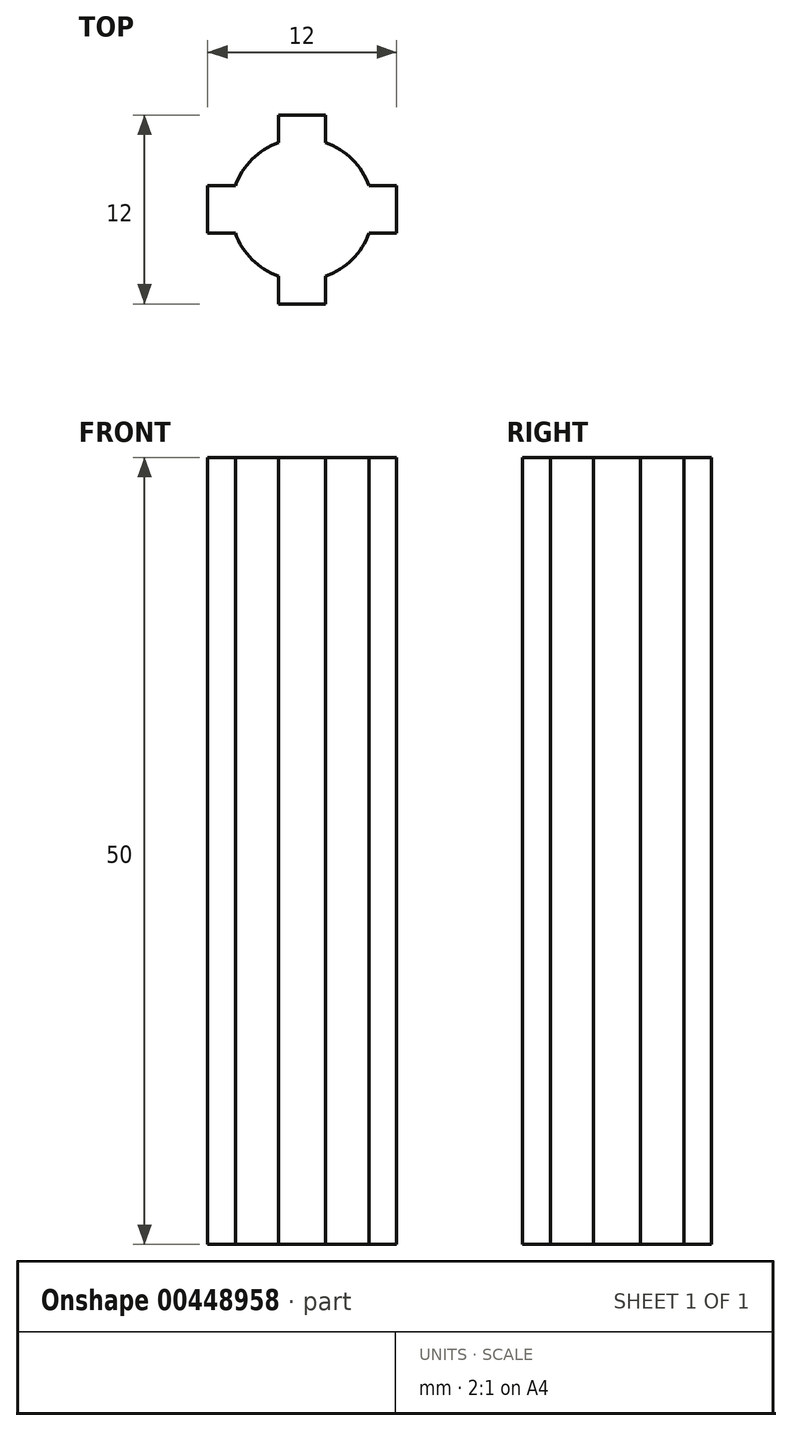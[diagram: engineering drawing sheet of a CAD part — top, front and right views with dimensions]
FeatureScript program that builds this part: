
annotation { "Feature Type Name" : "Feature", "Feature Type Description" : "" }
export const myFeature = defineFeature(function(context is Context, id is Id, definition is map)
    precondition{}
    {
        {
            var Q0;
            Q0=qCreatedBy(makeId("Top.planeOp"),FACE);
            var sketch = newSketch(context, id + "F0", { "sketchPlane" : qUnion([Q0])});
            skCircle(sketch, "E0", {"center": v(0, 0) * mm, "radius": 4.5 * mm});
            skLineSegment(sketch, "E1.bottom", {"start": v(6, -1.5) * mm, "end": v(-6, -1.5) * mm});
            skLineSegment(sketch, "E1.top", {"start": v(6, 1.5) * mm, "end": v(-6, 1.5) * mm});
            skLineSegment(sketch, "E1.left", {"start": v(6, -1.5) * mm, "end": v(6, 1.5) * mm});
            skLineSegment(sketch, "E1.right", {"start": v(-6, -1.5) * mm, "end": v(-6, 1.5) * mm});
            skLineSegment(sketch, "E2.bottom", {"start": v(-1.5, 6) * mm, "end": v(1.5, 6) * mm});
            skLineSegment(sketch, "E2.top", {"start": v(-1.5, -6) * mm, "end": v(1.5, -6) * mm});
            skLineSegment(sketch, "E2.left", {"start": v(-1.5, 6) * mm, "end": v(-1.5, -6) * mm});
            skLineSegment(sketch, "E2.right", {"start": v(1.5, 6) * mm, "end": v(1.5, -6) * mm});
            skSolve(sketch);
        }
        {
            var Q0;
            {var subQ5=sQuery(id+"F0.wireOp",EDGE,"E2.bottom");Q0=makeQuery(id+"F0.imprint","IMPRINT",FACE,{"disambiguationData":[TD([[makeQuery(id+"F0.imprint","IMPRINT",EDGE,{"derivedFrom":subQ5}),-1.0]])]});}
            var Q1;
            {var subQ5=sQuery(id+"F0.wireOp",EDGE,"E2.top");Q1=makeQuery(id+"F0.imprint","IMPRINT",FACE,{"disambiguationData":[TD([[makeQuery(id+"F0.imprint","IMPRINT",EDGE,{"derivedFrom":subQ5}),1.0]])]});}
            var Q2;
            {var subQ0=sQuery(id+"F0.wireOp",EDGE,"E2.right");var subQ1=sQuery(id+"F0.wireOp",EDGE,"E1.bottom");var subQ2=makeQuery(id+"F0.imprint","INTERSECT",VERTEX,{"derivedFrom":[subQ1,subQ0]});Q2=makeQuery(id+"F0.imprint","IMPRINT",FACE,{"disambiguationData":[TD([[makeQuery(id+"F0.imprint","IMPRINT",EDGE,{"disambiguationData":[TD([[subQ2,-1.0]])],"derivedFrom":subQ1}),-1.0]])]});}
            var Q3;
            {var subQ0=sQuery(id+"F0.wireOp",EDGE,"E2.left");var subQ1=sQuery(id+"F0.wireOp",EDGE,"E0");var subQ2=makeQuery(id+"F0.imprint","INTERSECT",VERTEX,{"disambiguationData":[OD(1.0)],"derivedFrom":[subQ1,subQ0]});Q3=makeQuery(id+"F0.imprint","IMPRINT",FACE,{"disambiguationData":[TD([[makeQuery(id+"F0.imprint","IMPRINT",EDGE,{"disambiguationData":[TD([[subQ2,-1.0]])],"derivedFrom":subQ1}),1.0]])]});}
            var Q4;
            {var subQ0=sQuery(id+"F0.wireOp",EDGE,"E2.right");var subQ1=sQuery(id+"F0.wireOp",EDGE,"E0");var subQ2=makeQuery(id+"F0.imprint","INTERSECT",VERTEX,{"disambiguationData":[OD(0.0)],"derivedFrom":[subQ1,subQ0]});Q4=makeQuery(id+"F0.imprint","IMPRINT",FACE,{"disambiguationData":[TD([[makeQuery(id+"F0.imprint","IMPRINT",EDGE,{"disambiguationData":[TD([[subQ2,-1.0]])],"derivedFrom":subQ1}),1.0]])]});}
            var Q5;
            {var subQ0=sQuery(id+"F0.wireOp",EDGE,"E2.right");var subQ1=sQuery(id+"F0.wireOp",EDGE,"E0");var subQ2=makeQuery(id+"F0.imprint","INTERSECT",VERTEX,{"disambiguationData":[OD(0.0)],"derivedFrom":[subQ1,subQ0]});Q5=makeQuery(id+"F0.imprint","IMPRINT",FACE,{"disambiguationData":[TD([[makeQuery(id+"F0.imprint","IMPRINT",EDGE,{"disambiguationData":[TD([[subQ2,1.0]])],"derivedFrom":subQ1}),1.0]])]});}
            var Q6;
            {var subQ0=sQuery(id+"F0.wireOp",EDGE,"E1.top");var subQ1=sQuery(id+"F0.wireOp",EDGE,"E0");var subQ2=makeQuery(id+"F0.imprint","INTERSECT",VERTEX,{"disambiguationData":[OD(0.0)],"derivedFrom":[subQ1,subQ0]});Q6=makeQuery(id+"F0.imprint","IMPRINT",FACE,{"disambiguationData":[TD([[makeQuery(id+"F0.imprint","IMPRINT",EDGE,{"disambiguationData":[TD([[subQ2,1.0]])],"derivedFrom":subQ1}),1.0]])]});}
            var Q7;
            {var subQ0=sQuery(id+"F0.wireOp",EDGE,"E2.right");var subQ1=sQuery(id+"F0.wireOp",EDGE,"E0");var subQ2=makeQuery(id+"F0.imprint","INTERSECT",VERTEX,{"disambiguationData":[OD(1.0)],"derivedFrom":[subQ1,subQ0]});Q7=makeQuery(id+"F0.imprint","IMPRINT",FACE,{"disambiguationData":[TD([[makeQuery(id+"F0.imprint","IMPRINT",EDGE,{"disambiguationData":[TD([[subQ2,-1.0]])],"derivedFrom":subQ1}),1.0]])]});}
            var Q8;
            {var subQ0=sQuery(id+"F0.wireOp",EDGE,"E1.bottom");var subQ1=sQuery(id+"F0.wireOp",EDGE,"E0");var subQ2=makeQuery(id+"F0.imprint","INTERSECT",VERTEX,{"disambiguationData":[OD(0.0)],"derivedFrom":[subQ1,subQ0]});Q8=makeQuery(id+"F0.imprint","IMPRINT",FACE,{"disambiguationData":[TD([[makeQuery(id+"F0.imprint","IMPRINT",EDGE,{"disambiguationData":[TD([[subQ2,-1.0]])],"derivedFrom":subQ1}),1.0]])]});}
            var Q9;
            {var subQ0=sQuery(id+"F0.wireOp",EDGE,"E1.top");var subQ1=sQuery(id+"F0.wireOp",EDGE,"E0");var subQ2=makeQuery(id+"F0.imprint","INTERSECT",VERTEX,{"disambiguationData":[OD(1.0)],"derivedFrom":[subQ1,subQ0]});Q9=makeQuery(id+"F0.imprint","IMPRINT",FACE,{"disambiguationData":[TD([[makeQuery(id+"F0.imprint","IMPRINT",EDGE,{"disambiguationData":[TD([[subQ2,-1.0]])],"derivedFrom":subQ1}),1.0]])]});}
            var Q10;
            {var subQ0=sQuery(id+"F0.wireOp",EDGE,"E2.left");var subQ1=sQuery(id+"F0.wireOp",EDGE,"E0");var subQ2=makeQuery(id+"F0.imprint","INTERSECT",VERTEX,{"disambiguationData":[OD(0.0)],"derivedFrom":[subQ1,subQ0]});Q10=makeQuery(id+"F0.imprint","IMPRINT",FACE,{"disambiguationData":[TD([[makeQuery(id+"F0.imprint","IMPRINT",EDGE,{"disambiguationData":[TD([[subQ2,-1.0]])],"derivedFrom":subQ1}),1.0]])]});}
            var Q11;
            {var subQ5=sQuery(id+"F0.wireOp",EDGE,"E1.right");Q11=makeQuery(id+"F0.imprint","IMPRINT",FACE,{"disambiguationData":[TD([[makeQuery(id+"F0.imprint","IMPRINT",EDGE,{"derivedFrom":subQ5}),-1.0]])]});}
            var Q12;
            {var subQ5=sQuery(id+"F0.wireOp",EDGE,"E1.left");Q12=makeQuery(id+"F0.imprint","IMPRINT",FACE,{"disambiguationData":[TD([[makeQuery(id+"F0.imprint","IMPRINT",EDGE,{"derivedFrom":subQ5}),1.0]])]});}
            extrude(context, id + "F1", {"entities" : qUnion([Q0, Q1, Q2, Q3, Q4, Q5, Q6, Q7, Q8, Q9, Q10, Q11, Q12]), "depth" : 50 * mm});
        }
    });
